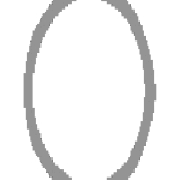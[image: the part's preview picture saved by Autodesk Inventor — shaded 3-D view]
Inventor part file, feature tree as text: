
AUTODESK INVENTOR PART (.ipt)
format: ipt  version: 2021 (Build 250183000, 183)  size: 109,056 bytes
history: native  units: in
note: dims shown in document units (in); Inventor stores cm internally (conversion verified against a paired STEP export)
features: other x4, sketch x3, plane x1
ambient origin geometry x8: Origin, YZ Plane, XZ Plane, XY Plane, X Axis, Y Axis, Z Axis, Center Point
bodies: Solid1 (feature_tree), Body (feature_tree)
feature tree (8):
  other  "Driven Length"
  other  "Frame Generator"
  other  "Start Plane"
  other  "End Plane"
  sketch  "Sketch"  dims[d2=39.5601in d4=-0.0in d5=39.5601in d6=0.12in d7=0.0in d8=90.0deg d9=39.5601in]
  sketch  "Sketch2"  dims[d0=1.0in]
  plane  "Work Plane3"
  sketch  "Sketch3"  dims[d1=0.065in]
